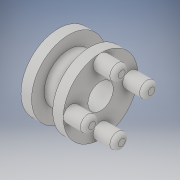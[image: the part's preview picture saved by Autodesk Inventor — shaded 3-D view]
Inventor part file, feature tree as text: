
AUTODESK INVENTOR PART (.ipt)
format: ipt  version: 2019 (Build 230136000, 136)  size: 175,104 bytes
history: native  units: in
note: dims shown in document units (in); Inventor stores cm internally (conversion verified against a paired STEP export)
features: fillet x4, sketch x3, revolve x1, extrude x1
ambient origin geometry x8: Origin, YZ Plane, XZ Plane, XY Plane, X Axis, Y Axis, Z Axis, Center Point
bodies: Body1 (feature_tree)
feature tree (9):
  sketch  "Sketch3"  dims[d10=0.3465in d11=0.3937in]
  sketch  "Sketch4"  dims[d12=0.0984in d13=0.1181in d14=0.1969in d15=90.0deg d24=0.2362in d25=0.2283in]
  revolve  "Revolution1"  [1 undecoded]
  extrude  "Extrusion4"  Depth=0.1181in
  fillet  "Fillet1"  Radius=0.1969in
  fillet  "Fillet2"  [1 undecoded]
  fillet  "Fillet3"  Radius=0.2362in
  fillet  "Fillet4"  Radius=0.2283in
  sketch  "Sketch7"  dims[d27=0.1417in d28=0.1417in d29=0.1417in d30=0.1417in d32=0.1969in d33=0.0in d34=0.0394in d35=0.0394in d36=0.0394in d37=0.0394in]
note: 2 required parameter values undecoded (feature->parameter linkage not recoverable at this tier; creation-order binding heuristic only, values carry confidence <= 0.55)